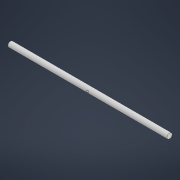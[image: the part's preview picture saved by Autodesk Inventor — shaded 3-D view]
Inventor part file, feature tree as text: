
AUTODESK INVENTOR PART (.ipt)
format: ipt  version: 2022 (Build 260153000, 153)  size: 106,496 bytes
history: native  units: in
note: dims shown in document units (in); Inventor stores cm internally (conversion verified against a paired STEP export)
features: sketch x3, extrude x2, fillet x1
ambient origin geometry x8: Origin, YZ Plane, XZ Plane, XY Plane, X Axis, Y Axis, Z Axis, Center Point
bodies: Solid1 (feature_tree)
feature tree (6):
  extrude  "Extrusion1"  Depth=1.0in
  extrude  "Extrusion2"  Depth=1.0in TaperAngle=0.0deg
  sketch  "Sketch3"  dims[d6=1.0in d7=0.0in d8=0.5in d9=0.0in d10=0.0in d11=0.0in]
  fillet  "Fillet1"  Radius=0.3937in
  sketch  "Sketch1"  dims[d0=31.4961in d1=1.0in]
  sketch  "Sketch2"  dims[d2=0.3937in d3=1.0in d4=0.0in d5=0.3937in]
